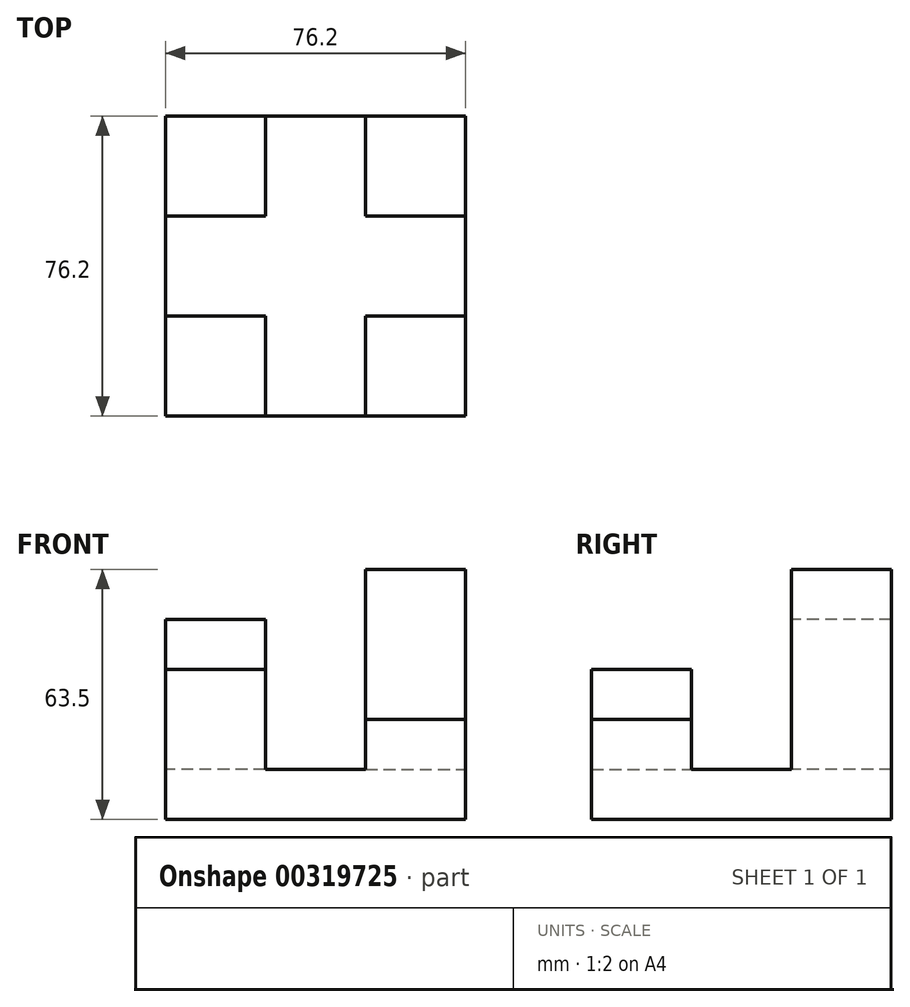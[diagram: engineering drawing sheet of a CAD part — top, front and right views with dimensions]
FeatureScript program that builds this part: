
annotation { "Feature Type Name" : "Feature", "Feature Type Description" : "" }
export const myFeature = defineFeature(function(context is Context, id is Id, definition is map)
    precondition{}
    {
        {
            var Q0;
            Q0=qCreatedBy(makeId("Top.planeOp"),FACE);
            var sketch = newSketch(context, id + "F0", { "sketchPlane" : qUnion([Q0])});
            skLineSegment(sketch, "E0", {"start": v(-28.3, 28.22) * mm, "end": v(-28.3, -47.98) * mm});
            skLineSegment(sketch, "E1", {"start": v(-28.3, -47.98) * mm, "end": v(47.9, -47.98) * mm});
            skLineSegment(sketch, "E2", {"start": v(47.9, -47.98) * mm, "end": v(47.9, 28.22) * mm});
            skLineSegment(sketch, "E3", {"start": v(47.9, 28.22) * mm, "end": v(-28.3, 28.22) * mm});
            skSolve(sketch);
        }
        {
            var Q0;
            Q0=makeQuery(id+"F0.imprint","IMPRINT",FACE,{"disambiguationData":[TD([[makeQuery(id+"F0.imprint","IMPRINT",EDGE,{"derivedFrom":sQuery(id+"F0.wireOp",EDGE,"E0")}),1.0]])]});
            extrude(context, id + "F1", {"entities" : qUnion([Q0]), "depth" : 12.7 * mm});
        }
        {
            var Q0;
            Q0=makeQuery(id+"F1.opExtrude","CAP_FACE",FACE,{"disambiguationData":[OSD([sQuery(id+"F0.wireOp",EDGE,"E0"),sQuery(id+"F0.wireOp",EDGE,"E1"),sQuery(id+"F0.wireOp",EDGE,"E2"),sQuery(id+"F0.wireOp",EDGE,"E3")])],"isStart":false});
            var sketch = newSketch(context, id + "F2", { "sketchPlane" : qUnion([Q0])});
            skLineSegment(sketch, "E4", {"start": v(22.5, 28.22) * mm, "end": v(22.5, 2.82) * mm});
            skLineSegment(sketch, "E5", {"start": v(47.9, 2.82) * mm, "end": v(22.5, 2.82) * mm});
            skLineSegment(sketch, "E6", {"start": v(-2.9, 28.22) * mm, "end": v(-2.9, 2.82) * mm});
            skLineSegment(sketch, "E7", {"start": v(-2.9, 2.82) * mm, "end": v(-28.3, 2.82) * mm});
            skLineSegment(sketch, "E8", {"start": v(-28.3, -22.58) * mm, "end": v(-2.9, -22.58) * mm});
            skLineSegment(sketch, "E9", {"start": v(-2.9, -22.58) * mm, "end": v(-2.9, -47.98) * mm});
            skLineSegment(sketch, "E10", {"start": v(22.5, -47.98) * mm, "end": v(22.5, -22.58) * mm});
            skLineSegment(sketch, "E11", {"start": v(22.5, -22.58) * mm, "end": v(47.9, -22.58) * mm});
            skSolve(sketch);
        }
        {
            var Q0;
            {var subQ0=sQuery(id+"F2.wireOp",EDGE,"E10");Q0=makeQuery(id+"F2.imprint","IMPRINT",FACE,{"disambiguationData":[TD([[makeQuery(id+"F2.imprint","IMPRINT",EDGE,{"derivedFrom":subQ0}),-1.0]])]});}
            var Q1;
            {var subQ0=sQuery(id+"F2.wireOp",EDGE,"E8");Q1=makeQuery(id+"F2.imprint","IMPRINT",FACE,{"disambiguationData":[TD([[makeQuery(id+"F2.imprint","IMPRINT",EDGE,{"derivedFrom":subQ0}),-1.0]])]});}
            var Q2;
            {var subQ0=sQuery(id+"F2.wireOp",EDGE,"E6");Q2=makeQuery(id+"F2.imprint","IMPRINT",FACE,{"disambiguationData":[TD([[makeQuery(id+"F2.imprint","IMPRINT",EDGE,{"derivedFrom":subQ0}),-1.0]])]});}
            var Q3;
            {var subQ0=sQuery(id+"F2.wireOp",EDGE,"E4");Q3=makeQuery(id+"F2.imprint","IMPRINT",FACE,{"disambiguationData":[TD([[makeQuery(id+"F2.imprint","IMPRINT",EDGE,{"derivedFrom":subQ0}),1.0]])]});}
            extrude(context, id + "F3", {"entities" : qUnion([Q0, Q1, Q2, Q3]), "operationType" : NewBodyOperationType.ADD, "depth" : 12.7 * mm});
        }
        {
            var Q0;
            Q0=makeQuery(id+"F3.opExtrude","CAP_FACE",FACE,{"disambiguationData":[OSD([sQuery(id+"F0.wireOp",EDGE,"E0"),sQuery(id+"F0.wireOp",EDGE,"E1"),sQuery(id+"F2.wireOp",EDGE,"E8"),sQuery(id+"F2.wireOp",EDGE,"E9")])],"isStart":false});
            extrude(context, id + "F4", {"entities" : qUnion([Q0]), "operationType" : NewBodyOperationType.ADD, "depth" : 12.7 * mm});
        }
        {
            var Q0;
            Q0=makeQuery(id+"F3.opExtrude","CAP_FACE",FACE,{"disambiguationData":[OSD([sQuery(id+"F0.wireOp",EDGE,"E0"),sQuery(id+"F0.wireOp",EDGE,"E3"),sQuery(id+"F2.wireOp",EDGE,"E6"),sQuery(id+"F2.wireOp",EDGE,"E7")])],"isStart":false});
            extrude(context, id + "F5", {"entities" : qUnion([Q0]), "operationType" : NewBodyOperationType.ADD, "depth" : 25.4 * mm});
        }
        {
            var Q0;
            Q0=makeQuery(id+"F3.opExtrude","CAP_FACE",FACE,{"disambiguationData":[OSD([sQuery(id+"F0.wireOp",EDGE,"E2"),sQuery(id+"F0.wireOp",EDGE,"E3"),sQuery(id+"F2.wireOp",EDGE,"E4"),sQuery(id+"F2.wireOp",EDGE,"E5")])],"isStart":false});
            extrude(context, id + "F6", {"entities" : qUnion([Q0]), "operationType" : NewBodyOperationType.ADD, "depth" : 38.1 * mm});
        }
    });
